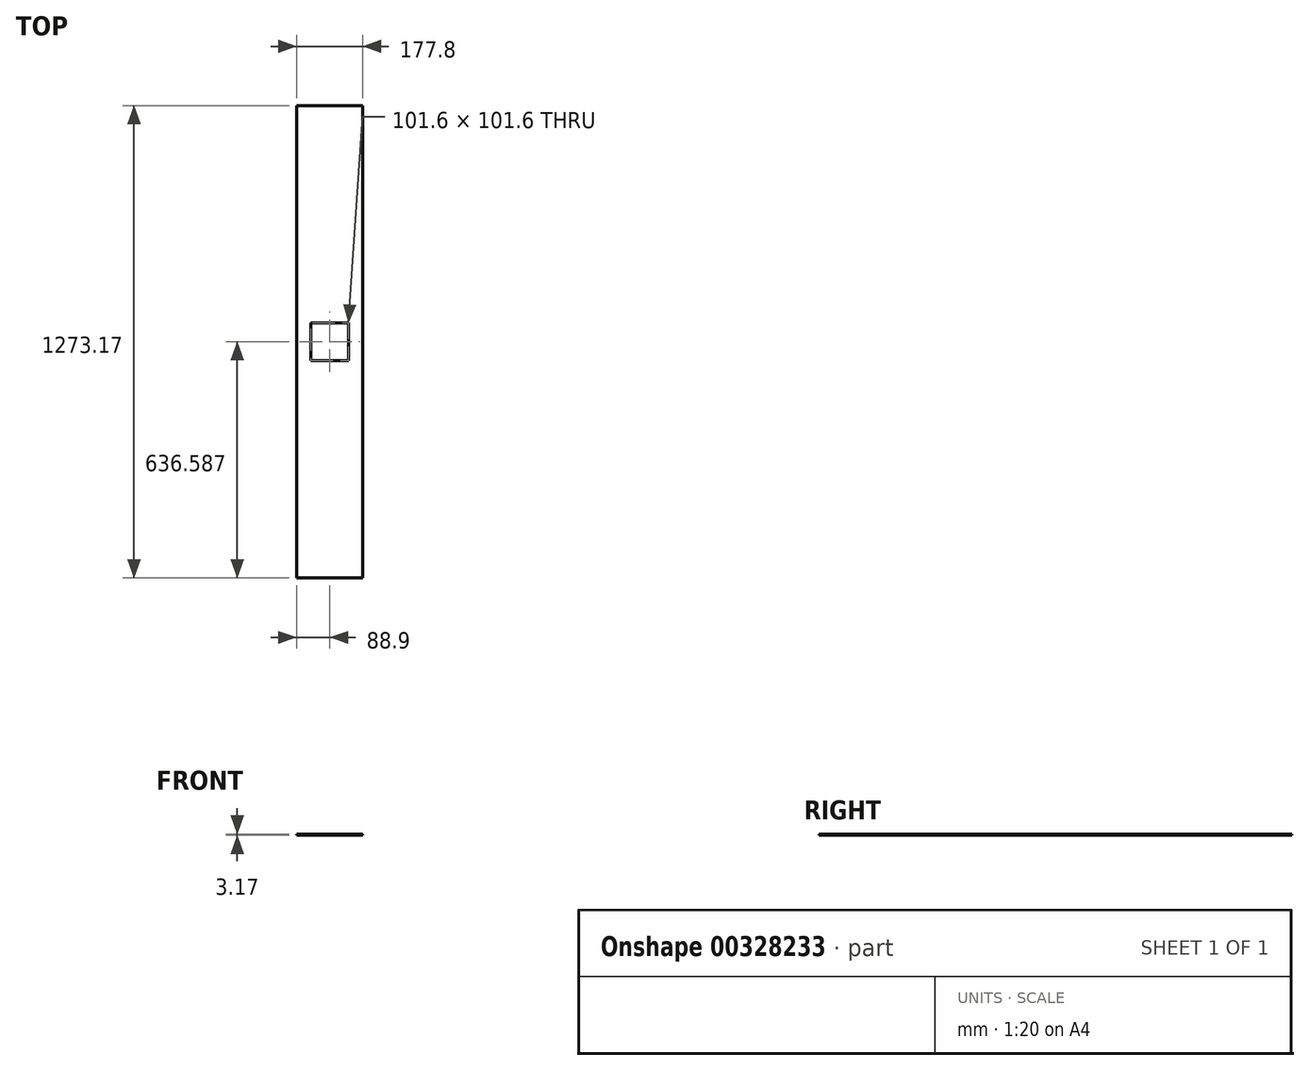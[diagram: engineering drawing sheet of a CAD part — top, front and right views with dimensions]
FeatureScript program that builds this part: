
annotation { "Feature Type Name" : "Feature", "Feature Type Description" : "" }
export const myFeature = defineFeature(function(context is Context, id is Id, definition is map)
    precondition{}
    {
        {
            var Q0;
            Q0=qCreatedBy(makeId("Top.planeOp"),FACE);
            var sketch = newSketch(context, id + "F0", { "sketchPlane" : qUnion([Q0])});
            skLineSegment(sketch, "E0", {"start": v(0, 0) * mm, "end": v(0, 1273.18) * mm});
            skLineSegment(sketch, "E1", {"start": v(0, 1273.18) * mm, "end": v(-177.8, 1273.18) * mm});
            skLineSegment(sketch, "E2", {"start": v(-177.8, 1273.18) * mm, "end": v(-177.8, 0) * mm});
            skLineSegment(sketch, "E3", {"start": v(-177.8, 0) * mm, "end": v(0, 0) * mm});
            skLineSegment(sketch, "E4", {"start": v(-88.9, 1273.18) * mm, "end": v(-88.9, 0) * mm, "construction": true});
            skLineSegment(sketch, "E5.bottom", {"start": v(-139.7, 687.39) * mm, "end": v(-38.1, 687.39) * mm});
            skLineSegment(sketch, "E5.top", {"start": v(-139.7, 585.79) * mm, "end": v(-38.1, 585.79) * mm});
            skLineSegment(sketch, "E5.left", {"start": v(-139.7, 687.39) * mm, "end": v(-139.7, 585.79) * mm});
            skLineSegment(sketch, "E5.right", {"start": v(-38.1, 687.39) * mm, "end": v(-38.1, 585.79) * mm});
            skPoint(sketch, "E5.middle", {"position": v(-88.9, 636.59) * mm});
            skSolve(sketch);
        }
        {
            var Q0;
            Q0=makeQuery(id+"F0.imprint","IMPRINT",FACE,{"disambiguationData":[TD([[makeQuery(id+"F0.imprint","IMPRINT",EDGE,{"derivedFrom":sQuery(id+"F0.wireOp",EDGE,"E0")}),1.0]])]});
            extrude(context, id + "F1", {"entities" : qUnion([Q0]), "depth" : 3.17 * mm});
        }
    });
